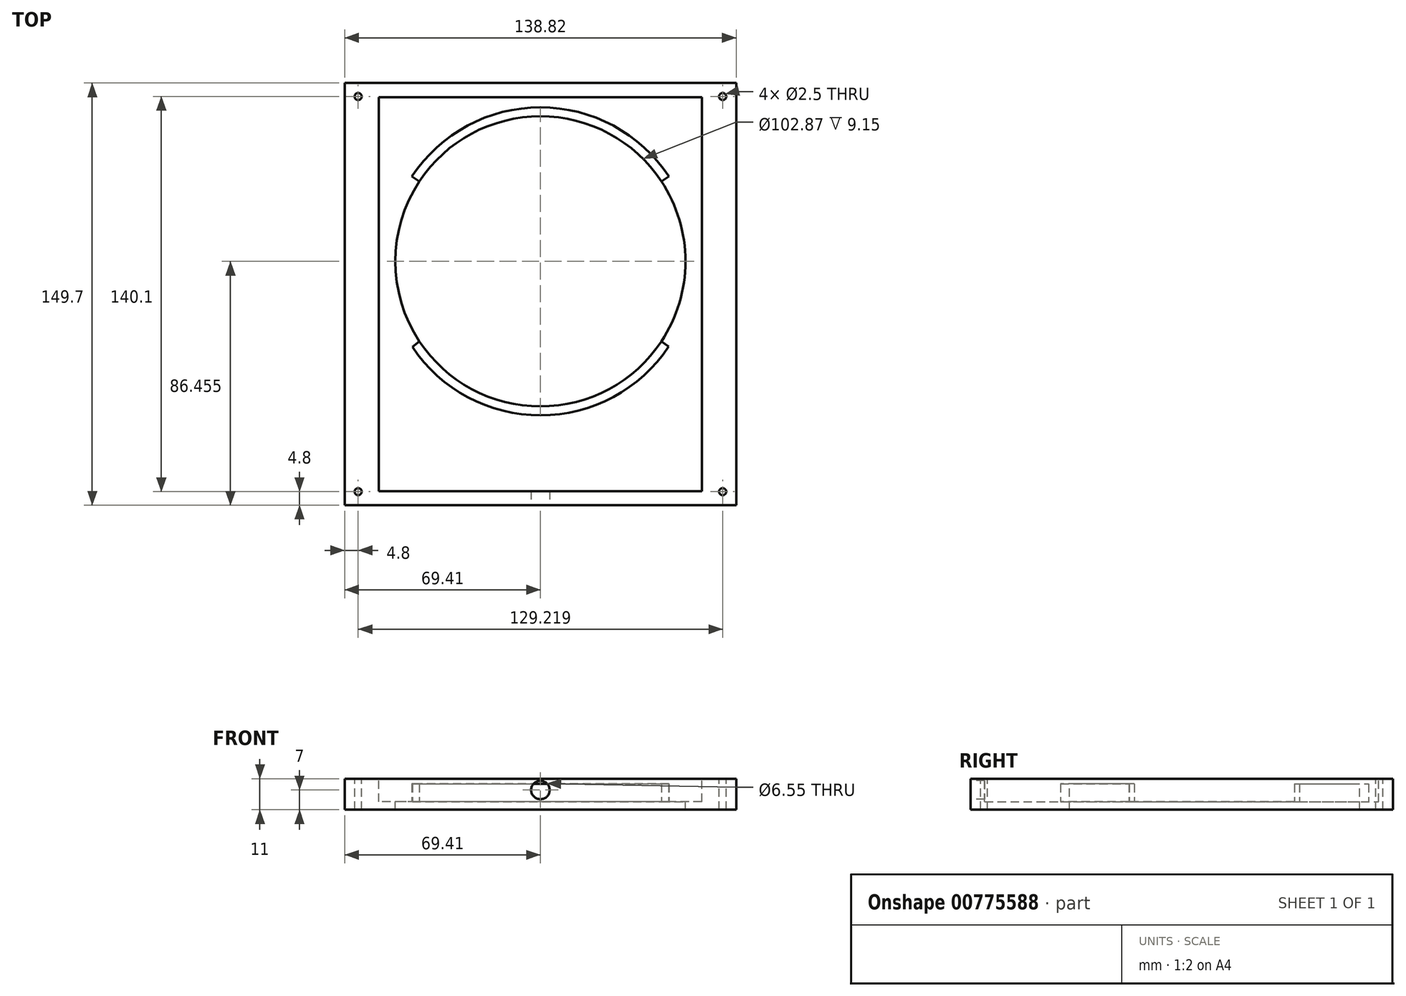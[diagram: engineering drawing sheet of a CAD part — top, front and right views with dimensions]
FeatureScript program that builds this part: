
annotation { "Feature Type Name" : "Feature", "Feature Type Description" : "" }
export const myFeature = defineFeature(function(context is Context, id is Id, definition is map)
    precondition{}
    {
        {
            var Q0;
            Q0=qCreatedBy(makeId("Top.planeOp"),FACE);
            var sketch = newSketch(context, id + "F0", { "sketchPlane" : qUnion([Q0])});
            skLineSegment(sketch, "E0.bottom", {"start": v(69.4, -74.85) * mm, "end": v(-69.4, -74.85) * mm});
            skLineSegment(sketch, "E0.top", {"start": v(69.4, 74.85) * mm, "end": v(-69.4, 74.85) * mm});
            skLineSegment(sketch, "E0.left", {"start": v(69.4, -74.85) * mm, "end": v(69.4, 74.85) * mm});
            skLineSegment(sketch, "E0.right", {"start": v(-69.4, -74.85) * mm, "end": v(-69.4, 74.85) * mm});
            skPoint(sketch, "E0.middle", {"position": v(0, 0) * mm});
            skSolve(sketch);
        }
        {
            var Q0;
            Q0 = qSketchRegion(id + "F0", true);
            extrude(context, id + "F1", {"entities" : qUnion([Q0]), "depth" : 8 * mm + 3 * mm, "offsetDistance" : 25.4 * mm});
        }
        {
            var Q0;
            Q0=makeQuery(id+"F1.opExtrude","CAP_FACE",FACE,{"disambiguationData":[OSD([sQuery(id+"F0.wireOp",EDGE,"E0.bottom"),sQuery(id+"F0.wireOp",EDGE,"E0.top"),sQuery(id+"F0.wireOp",EDGE,"E0.left"),sQuery(id+"F0.wireOp",EDGE,"E0.right")])],"isStart":false});
            var sketch = newSketch(context, id + "F2", { "sketchPlane" : qUnion([Q0])});
            skCircle(sketch, "E1", {"center": v(0, 11.6) * mm, "radius": 51.44 * mm});
            skCircle(sketch, "E2", {"center": v(-64.6, 70.05) * mm, "radius": 1.25 * mm});
            skCircle(sketch, "E3", {"center": v(64.6, 70.05) * mm, "radius": 1.25 * mm});
            skCircle(sketch, "E4", {"center": v(64.6, -70.05) * mm, "radius": 1.25 * mm});
            skCircle(sketch, "E5", {"center": v(-64.6, -70.05) * mm, "radius": 1.25 * mm});
            skLineSegment(sketch, "E6", {"start": v(-69.4, 0) * mm, "end": v(69.4, 0) * mm});
            skSolve(sketch);
        }
        {
            var Q0;
            Q0 = qSketchRegion(id + "F2", true);
            extrude(context, id + "F3", {"entities" : qUnion([Q0]), "operationType" : NewBodyOperationType.REMOVE, "endBound" : BoundingType.UP_TO_NEXT, "oppositeDirection" : true, "depth" : 25.4 * mm, "offsetDistance" : 25.4 * mm});
        }
        {
            var Q0;
            Q0=makeQuery(id+"F1.opExtrude","CAP_FACE",FACE,{"disambiguationData":[OSD([sQuery(id+"F0.wireOp",EDGE,"E0.bottom"),sQuery(id+"F0.wireOp",EDGE,"E0.top"),sQuery(id+"F0.wireOp",EDGE,"E0.left"),sQuery(id+"F0.wireOp",EDGE,"E0.right")])],"isStart":false});
            var sketch = newSketch(context, id + "F4", { "sketchPlane" : qUnion([Q0])});
            skLineSegment(sketch, "E7.bottom", {"start": v(57.25, -69.85) * mm, "end": v(-57.25, -69.85) * mm});
            skLineSegment(sketch, "E7.top", {"start": v(57.25, 69.85) * mm, "end": v(-57.25, 69.85) * mm});
            skLineSegment(sketch, "E7.left", {"start": v(57.25, -69.85) * mm, "end": v(57.25, 69.85) * mm});
            skLineSegment(sketch, "E7.right", {"start": v(-57.25, -69.85) * mm, "end": v(-57.25, 69.85) * mm});
            skPoint(sketch, "E7.middle", {"position": v(0, 0) * mm});
            skSolve(sketch);
        }
        {
            var Q0;
            Q0 = qSketchRegion(id + "F4", true);
            extrude(context, id + "F5", {"entities" : qUnion([Q0]), "operationType" : NewBodyOperationType.REMOVE, "oppositeDirection" : true, "depth" : 8 * mm + 0.2 * mm, "offsetDistance" : 25.4 * mm});
        }
        {
            var Q0;
            Q0=makeQuery(id+"F1.opExtrude","SWEPT_FACE",FACE,{"disambiguationData":[OSD([sQuery(id+"F0.wireOp",EDGE,"E0.bottom")])]});
            var sketch = newSketch(context, id + "F6", { "sketchPlane" : qUnion([Q0])});
            skCircle(sketch, "E8", {"center": v(0, 7) * mm, "radius": 3.28 * mm});
            skSolve(sketch);
        }
        {
            var Q0;
            Q0 = qSketchRegion(id + "F6", true);
            extrude(context, id + "F7", {"entities" : qUnion([Q0]), "operationType" : NewBodyOperationType.REMOVE, "endBound" : BoundingType.UP_TO_NEXT, "oppositeDirection" : true, "depth" : 25.4 * mm, "offsetDistance" : 25.4 * mm});
        }
        {
            var Q0;
            Q0=makeQuery(id+"F5.boolean.opBoolean","COPY",FACE,{"derivedFrom":makeQuery(id+"F5.opExtrude","CAP_FACE",FACE,{"disambiguationData":[OSD([sQuery(id+"F4.wireOp",EDGE,"E7.bottom"),sQuery(id+"F4.wireOp",EDGE,"E7.top"),sQuery(id+"F4.wireOp",EDGE,"E7.left"),sQuery(id+"F4.wireOp",EDGE,"E7.right")])],"isStart":false})});
            var sketch = newSketch(context, id + "F8", { "sketchPlane" : qUnion([Q0])});
            skArc(sketch, "E9", {"start": v(42.9, 39.97) * mm, "mid": v(0, 63.04) * mm, "end": v(-42.9, 39.97) * mm});
            skLineSegment(sketch, "E10", {"start": v(42.9, 39.97) * mm, "end": v(45.55, 41.73) * mm});
            skLineSegment(sketch, "E11", {"start": v(-42.9, 39.97) * mm, "end": v(-45.55, 41.73) * mm});
            skLineSegment(sketch, "E12", {"start": v(0, 69.85) * mm, "end": v(0, -69.85) * mm});
            skArc(sketch, "E13", {"start": v(45.55, 41.73) * mm, "mid": v(0, 66.22) * mm, "end": v(-45.55, 41.73) * mm});
            skArc(sketch, "E14", {"start": v(-42.9, -16.76) * mm, "mid": v(0, -39.83) * mm, "end": v(42.9, -16.76) * mm});
            skLineSegment(sketch, "E15", {"start": v(42.9, -16.76) * mm, "end": v(45.49, -18.61) * mm});
            skLineSegment(sketch, "E16", {"start": v(-42.9, -16.76) * mm, "end": v(-45.38, -18.75) * mm});
            skArc(sketch, "E17", {"start": v(-45.38, -18.75) * mm, "mid": v(0.1, -43) * mm, "end": v(45.49, -18.61) * mm});
            skSolve(sketch);
        }
        {
            var Q0;
            Q0 = qSketchRegion(id + "F8", true);
            extrude(context, id + "F9", {"entities" : qUnion([Q0]), "operationType" : NewBodyOperationType.ADD, "depth" : 6.35 * mm, "offsetDistance" : 25.4 * mm});
        }
    });
